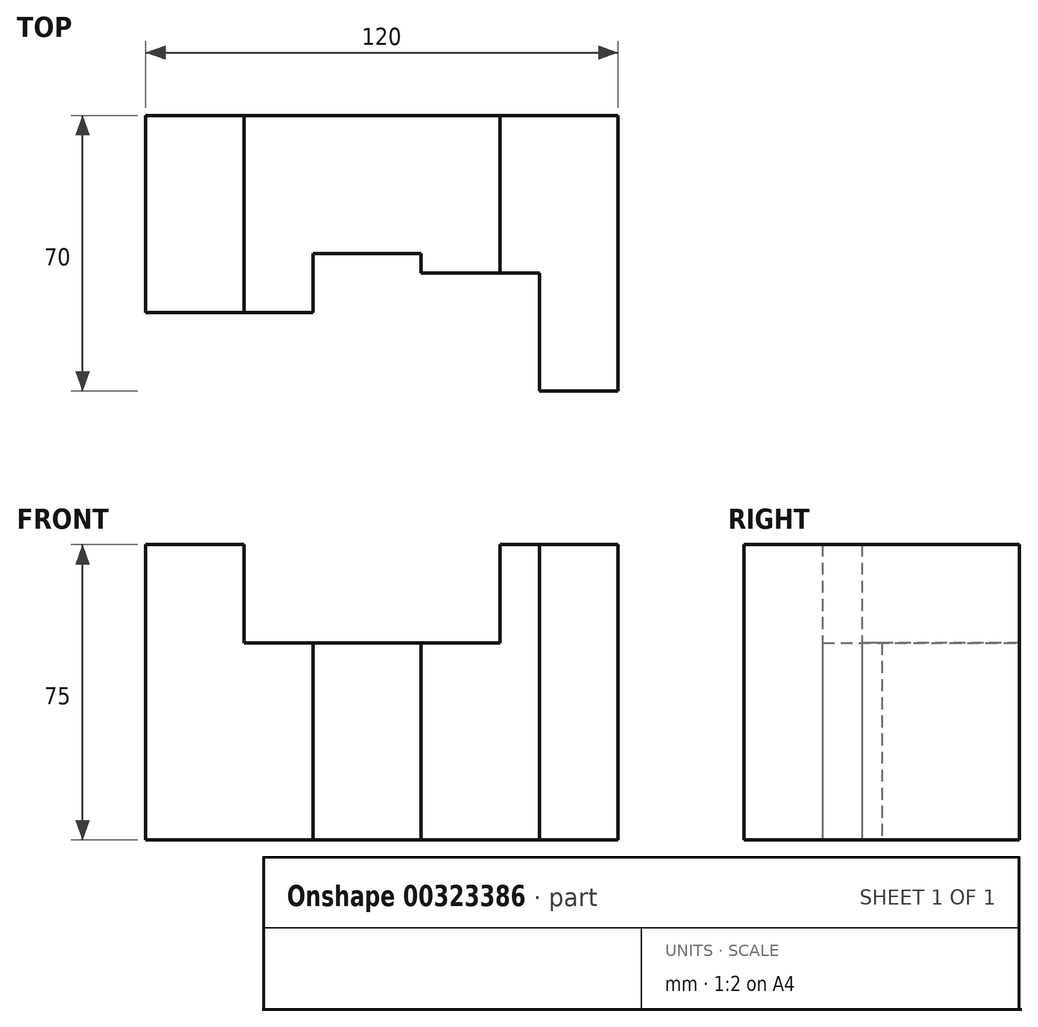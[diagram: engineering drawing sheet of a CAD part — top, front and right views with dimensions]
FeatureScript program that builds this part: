
annotation { "Feature Type Name" : "Feature", "Feature Type Description" : "" }
export const myFeature = defineFeature(function(context is Context, id is Id, definition is map)
    precondition{}
    {
        {
            var Q0;
            Q0=qCreatedBy(makeId("Top.planeOp"),FACE);
            var sketch = newSketch(context, id + "F0", { "sketchPlane" : qUnion([Q0])});
            skLineSegment(sketch, "E0", {"start": v(0, 0) * mm, "end": v(25, 0) * mm});
            skLineSegment(sketch, "E1", {"start": v(25, 0) * mm, "end": v(25, 50) * mm});
            skLineSegment(sketch, "E2", {"start": v(25, 50) * mm, "end": v(0, 50) * mm});
            skLineSegment(sketch, "E3", {"start": v(0, 50) * mm, "end": v(0, 0) * mm});
            skLineSegment(sketch, "E4", {"start": v(25, 0) * mm, "end": v(42.5, 0) * mm});
            skLineSegment(sketch, "E5", {"start": v(42.5, 0) * mm, "end": v(42.5, 15) * mm});
            skLineSegment(sketch, "E6", {"start": v(42.5, 15) * mm, "end": v(70, 15) * mm});
            skLineSegment(sketch, "E7", {"start": v(100, 10) * mm, "end": v(100, -20) * mm});
            skLineSegment(sketch, "E8", {"start": v(100, -20) * mm, "end": v(120, -20) * mm});
            skLineSegment(sketch, "E9", {"start": v(120, -20) * mm, "end": v(120, 50) * mm});
            skLineSegment(sketch, "E10", {"start": v(120, 50) * mm, "end": v(25, 50) * mm});
            skLineSegment(sketch, "E11", {"start": v(70, 15) * mm, "end": v(70, 10) * mm});
            skLineSegment(sketch, "E12", {"start": v(70, 10) * mm, "end": v(100, 10) * mm});
            skSolve(sketch);
        }
        {
            var Q0;
            Q0 = qSketchRegion(id + "F0", true);
            extrude(context, id + "F1", {"entities" : qUnion([Q0]), "endBound" : BoundingType.SYMMETRIC, "depth" : 50 * mm});
        }
        {
            var Q0;
            Q0=makeQuery(id+"F1.opExtrude","CAP_FACE",FACE,{"disambiguationData":[OSD([sQuery(id+"F0.wireOp",EDGE,"E0"),sQuery(id+"F0.wireOp",EDGE,"E2"),sQuery(id+"F0.wireOp",EDGE,"E3"),sQuery(id+"F0.wireOp",EDGE,"E4"),sQuery(id+"F0.wireOp",EDGE,"E5"),sQuery(id+"F0.wireOp",EDGE,"E6"),sQuery(id+"F0.wireOp",EDGE,"E7"),sQuery(id+"F0.wireOp",EDGE,"E8"),sQuery(id+"F0.wireOp",EDGE,"E9"),sQuery(id+"F0.wireOp",EDGE,"E10"),sQuery(id+"F0.wireOp",EDGE,"E11"),sQuery(id+"F0.wireOp",EDGE,"E12")])],"isStart":false});
            var sketch = newSketch(context, id + "F2", { "sketchPlane" : qUnion([Q0])});
            skLineSegment(sketch, "E13", {"start": v(0, 0) * mm, "end": v(25, 0) * mm});
            skLineSegment(sketch, "E14", {"start": v(25, 0) * mm, "end": v(25, 50) * mm});
            skLineSegment(sketch, "E15", {"start": v(25, 50) * mm, "end": v(0, 50) * mm});
            skLineSegment(sketch, "E16", {"start": v(0, 50) * mm, "end": v(0, 0) * mm});
            skLineSegment(sketch, "E17", {"start": v(120, -20) * mm, "end": v(120, 50) * mm});
            skLineSegment(sketch, "E18", {"start": v(120, 50) * mm, "end": v(90, 50) * mm});
            skLineSegment(sketch, "E19", {"start": v(120, -20) * mm, "end": v(100, -20) * mm});
            skLineSegment(sketch, "E20", {"start": v(100, -20) * mm, "end": v(100, 10) * mm});
            skLineSegment(sketch, "E21", {"start": v(90, 50) * mm, "end": v(90, 10) * mm});
            skLineSegment(sketch, "E22", {"start": v(90, 10) * mm, "end": v(100, 10) * mm});
            skSolve(sketch);
        }
        {
            var Q0;
            Q0 = qSketchRegion(id + "F2", true);
            extrude(context, id + "F3", {"entities" : qUnion([Q0]), "operationType" : NewBodyOperationType.ADD, "depth" : 25 * mm});
        }
    });
